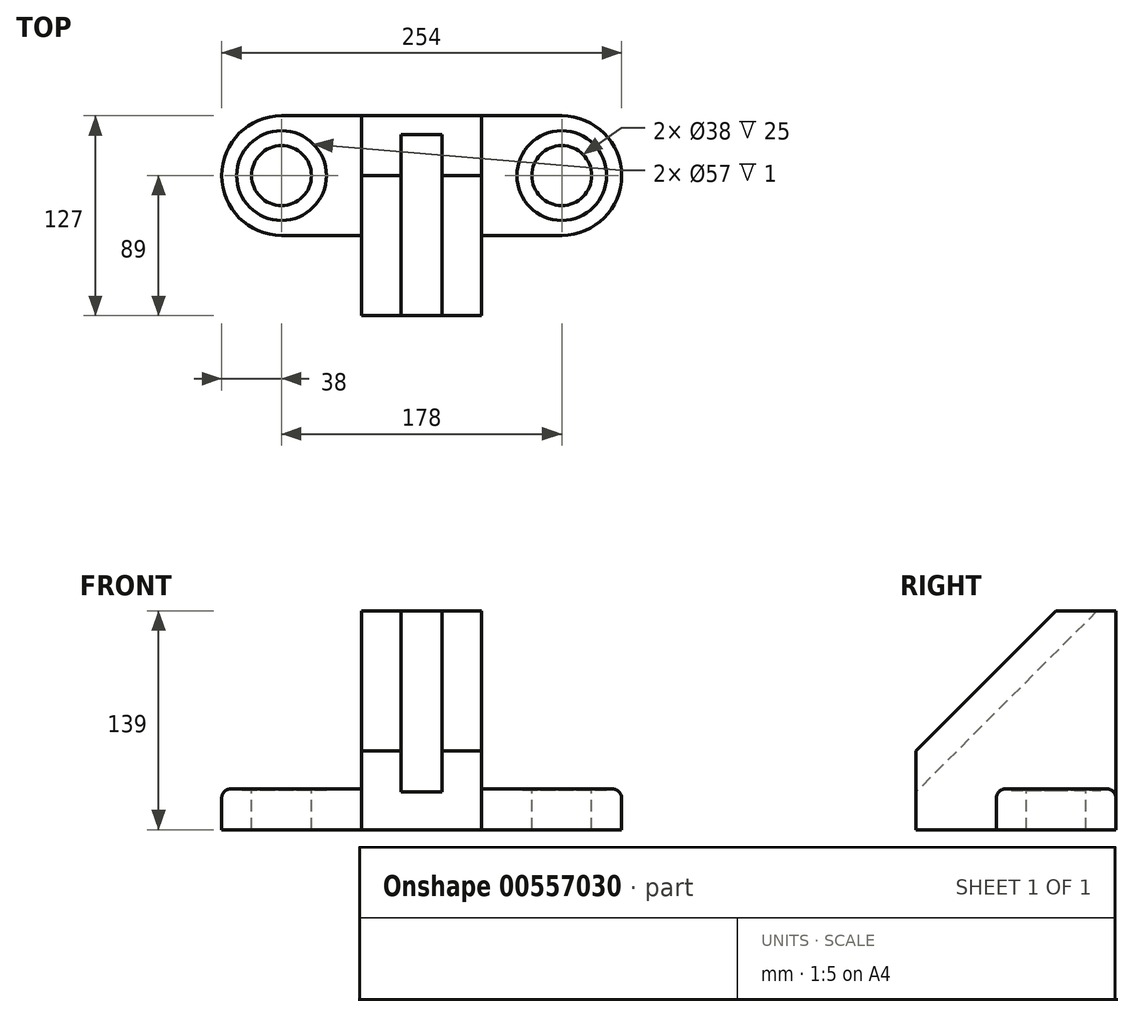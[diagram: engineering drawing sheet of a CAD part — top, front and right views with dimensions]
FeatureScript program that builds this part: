
annotation { "Feature Type Name" : "Feature", "Feature Type Description" : "" }
export const myFeature = defineFeature(function(context is Context, id is Id, definition is map)
    precondition{}
    {
        {
            var Q0;
            Q0=qCreatedBy(makeId("Right.planeOp"),FACE);
            var sketch = newSketch(context, id + "F0", { "sketchPlane" : qUnion([Q0])});
            skLineSegment(sketch, "E0.bottom", {"start": v(0, 0) * mm, "end": v(-127, 0) * mm});
            skLineSegment(sketch, "E0.top", {"start": v(0, -139) * mm, "end": v(-127, -139) * mm});
            skLineSegment(sketch, "E0.left", {"start": v(0, 0) * mm, "end": v(0, -139) * mm});
            skLineSegment(sketch, "E0.right", {"start": v(-127, 0) * mm, "end": v(-127, -139) * mm});
            skSolve(sketch);
        }
        {
            var Q0;
            Q0 = qSketchRegion(id + "F0", true);
            extrude(context, id + "F1", {"entities" : qUnion([Q0]), "depth" : 76 * mm, "offsetDistance" : 25 * mm});
        }
        {
            var Q0;
            Q0=makeQuery(id+"F1.opExtrude","CAP_FACE",FACE,{"disambiguationData":[OSD([sQuery(id+"F0.wireOp",EDGE,"E0.bottom"),sQuery(id+"F0.wireOp",EDGE,"E0.top"),sQuery(id+"F0.wireOp",EDGE,"E0.left"),sQuery(id+"F0.wireOp",EDGE,"E0.right")])],"isStart":true});
            var sketch = newSketch(context, id + "F2", { "sketchPlane" : qUnion([Q0])});
            skLineSegment(sketch, "E1.bottom", {"start": v(0, -139) * mm, "end": v(76, -139) * mm});
            skLineSegment(sketch, "E1.top", {"start": v(0, -113) * mm, "end": v(76, -113) * mm});
            skLineSegment(sketch, "E1.left", {"start": v(0, -139) * mm, "end": v(0, -113) * mm});
            skLineSegment(sketch, "E1.right", {"start": v(76, -139) * mm, "end": v(76, -113) * mm});
            skSolve(sketch);
        }
        {
            var Q0;
            Q0=makeQuery(id+"F1.opExtrude","CAP_FACE",FACE,{"disambiguationData":[OSD([sQuery(id+"F0.wireOp",EDGE,"E0.bottom"),sQuery(id+"F0.wireOp",EDGE,"E0.top"),sQuery(id+"F0.wireOp",EDGE,"E0.left"),sQuery(id+"F0.wireOp",EDGE,"E0.right")])],"isStart":false});
            var sketch = newSketch(context, id + "F3", { "sketchPlane" : qUnion([Q0])});
            skLineSegment(sketch, "E2.bottom", {"start": v(0, -139) * mm, "end": v(-76, -139) * mm});
            skLineSegment(sketch, "E2.top", {"start": v(0, -113) * mm, "end": v(-76, -113) * mm});
            skLineSegment(sketch, "E2.left", {"start": v(0, -139) * mm, "end": v(0, -113) * mm});
            skLineSegment(sketch, "E2.right", {"start": v(-76, -139) * mm, "end": v(-76, -113) * mm});
            skSolve(sketch);
        }
        {
            var Q0;
            Q0=makeQuery(id+"F3.imprint","IMPRINT",FACE,{"disambiguationData":[TD([[makeQuery(id+"F3.imprint","IMPRINT",EDGE,{"derivedFrom":sQuery(id+"F3.wireOp",EDGE,"E2.bottom")}),-1.0]])]});
            extrude(context, id + "F4", {"entities" : qUnion([Q0]), "operationType" : NewBodyOperationType.ADD, "depth" : 51 * mm, "offsetDistance" : 25 * mm});
        }
        {
            var Q0;
            Q0=makeQuery(id+"F2.imprint","IMPRINT",FACE,{"disambiguationData":[TD([[makeQuery(id+"F2.imprint","IMPRINT",EDGE,{"derivedFrom":sQuery(id+"F2.wireOp",EDGE,"E1.bottom")}),1.0]])]});
            extrude(context, id + "F5", {"entities" : qUnion([Q0]), "operationType" : NewBodyOperationType.ADD, "depth" : 51 * mm, "offsetDistance" : 25 * mm});
        }
        {
            var Q0;
            Q0=makeQuery(id+"F5.opExtrude","CAP_FACE",FACE,{"disambiguationData":[OSD([sQuery(id+"F2.wireOp",EDGE,"E1.bottom"),sQuery(id+"F2.wireOp",EDGE,"E1.top"),sQuery(id+"F2.wireOp",EDGE,"E1.left"),sQuery(id+"F2.wireOp",EDGE,"E1.right")])],"isStart":false});
            extrude(context, id + "F6", {"entities" : qUnion([Q0]), "operationType" : NewBodyOperationType.ADD, "depth" : 38 * mm, "offsetDistance" : 25 * mm});
        }
        {
            var Q0;
            Q0=makeQuery(id+"F4.opExtrude","CAP_FACE",FACE,{"disambiguationData":[OSD([sQuery(id+"F3.wireOp",EDGE,"E2.bottom"),sQuery(id+"F3.wireOp",EDGE,"E2.top"),sQuery(id+"F3.wireOp",EDGE,"E2.left"),sQuery(id+"F3.wireOp",EDGE,"E2.right")])],"isStart":false});
            extrude(context, id + "F7", {"entities" : qUnion([Q0]), "operationType" : NewBodyOperationType.ADD, "depth" : 38 * mm, "offsetDistance" : 25 * mm});
        }
        {
            var Q0;
            {var subQ0=sQuery(id+"F2.wireOp",EDGE,"E1.top");Q0=makeQuery(id+"F6.boolean.opBoolean","MERGE",FACE,{"derivedFrom":[makeQuery(id+"F5.opExtrude","SWEPT_FACE",FACE,{"disambiguationData":[OSD([subQ0])]}),makeQuery(id+"F6.opExtrude","SWEPT_FACE",FACE,{"disambiguationData":[OSD([subQ0])]})]});}
            var sketch = newSketch(context, id + "F8", { "sketchPlane" : qUnion([Q0])});
            skCircle(sketch, "E3", {"center": v(-51, -38) * mm, "radius": 19 * mm});
            skCircle(sketch, "E4", {"center": v(127, -38) * mm, "radius": 19 * mm});
            skSolve(sketch);
        }
        {
            var Q0;
            Q0=makeQuery(id+"F8.imprint","IMPRINT",FACE,{"disambiguationData":[TD([[makeQuery(id+"F8.imprint","IMPRINT",EDGE,{"derivedFrom":sQuery(id+"F8.wireOp",EDGE,"E3")}),1.0]])]});
            var Q1;
            Q1=makeQuery(id+"F8.imprint","IMPRINT",FACE,{"disambiguationData":[TD([[makeQuery(id+"F8.imprint","IMPRINT",EDGE,{"derivedFrom":sQuery(id+"F8.wireOp",EDGE,"E4")}),1.0]])]});
            extrude(context, id + "F9", {"entities" : qUnion([Q0, Q1]), "operationType" : NewBodyOperationType.REMOVE, "endBound" : BoundingType.THROUGH_ALL, "oppositeDirection" : true, "depth" : 25 * mm, "offsetDistance" : 25 * mm});
        }
        {
            var Q0;
            Q0=makeQuery(id+"F6.opExtrude","CAP_EDGE",EDGE,{"disambiguationData":[OSD([sQuery(id+"F2.wireOp",EDGE,"E1.left")])],"isStart":false});
            var Q1;
            Q1=makeQuery(id+"F6.opExtrude","CAP_EDGE",EDGE,{"disambiguationData":[OSD([sQuery(id+"F2.wireOp",EDGE,"E1.right")])],"isStart":false});
            var Q2;
            Q2=makeQuery(id+"F7.opExtrude","CAP_EDGE",EDGE,{"disambiguationData":[OSD([sQuery(id+"F3.wireOp",EDGE,"E2.right")])],"isStart":false});
            var Q3;
            Q3=makeQuery(id+"F7.opExtrude","CAP_EDGE",EDGE,{"disambiguationData":[OSD([sQuery(id+"F3.wireOp",EDGE,"E2.left")])],"isStart":false});
            fillet(context, id + "F10", {"entities" : qUnion([Q0, Q1, Q2, Q3]), "radius" : 38 * mm, "tangentPropagation" : true, "allowEdgeOverflow" : false});
        }
        {
            var Q0;
            {var subQ0=sQuery(id+"F2.wireOp",EDGE,"E1.top");Q0=makeQuery(id+"F6.boolean.opBoolean","MERGE",FACE,{"derivedFrom":[makeQuery(id+"F5.opExtrude","SWEPT_FACE",FACE,{"disambiguationData":[OSD([subQ0])]}),makeQuery(id+"F6.opExtrude","SWEPT_FACE",FACE,{"disambiguationData":[OSD([subQ0])]})]});}
            var sketch = newSketch(context, id + "F11", { "sketchPlane" : qUnion([Q0])});
            skCircle(sketch, "E5", {"center": v(-51, -38) * mm, "radius": 28.5 * mm});
            skSolve(sketch);
        }
        {
            var Q0;
            {var subQ0=sQuery(id+"F3.wireOp",EDGE,"E2.top");Q0=makeQuery(id+"F7.boolean.opBoolean","MERGE",FACE,{"derivedFrom":[makeQuery(id+"F4.opExtrude","SWEPT_FACE",FACE,{"disambiguationData":[OSD([subQ0])]}),makeQuery(id+"F7.opExtrude","SWEPT_FACE",FACE,{"disambiguationData":[OSD([subQ0])]})]});}
            var sketch = newSketch(context, id + "F12", { "sketchPlane" : qUnion([Q0])});
            skCircle(sketch, "E6", {"center": v(127, -38) * mm, "radius": 28.5 * mm});
            skSolve(sketch);
        }
        {
            var Q0;
            Q0=makeQuery(id+"F11.imprint","IMPRINT",FACE,{"disambiguationData":[TD([[makeQuery(id+"F11.imprint","IMPRINT",EDGE,{"derivedFrom":sQuery(id+"F11.wireOp",EDGE,"E5")}),1.0]])]});
            extrude(context, id + "F13", {"entities" : qUnion([Q0]), "operationType" : NewBodyOperationType.REMOVE, "oppositeDirection" : true, "depth" : 1 * mm, "offsetDistance" : 25 * mm});
        }
        {
            var Q0;
            Q0=makeQuery(id+"F12.imprint","IMPRINT",FACE,{"disambiguationData":[TD([[makeQuery(id+"F12.imprint","IMPRINT",EDGE,{"derivedFrom":sQuery(id+"F12.wireOp",EDGE,"E6")}),1.0]])]});
            extrude(context, id + "F14", {"entities" : qUnion([Q0]), "operationType" : NewBodyOperationType.REMOVE, "oppositeDirection" : true, "depth" : 1 * mm, "offsetDistance" : 25 * mm});
        }
        {
            var Q0;
            {var subQ0=sQuery(id+"F2.wireOp",EDGE,"E1.right");var subQ1=sQuery(id+"F2.wireOp",EDGE,"E1.top");Q0=makeQuery(id+"F6.boolean.opBoolean","MERGE",EDGE,{"derivedFrom":[makeQuery(id+"F5.opExtrude","SWEPT_EDGE",EDGE,{"disambiguationData":[OSD([subQ1,subQ0])]}),makeQuery(id+"F6.opExtrude","SWEPT_EDGE",EDGE,{"disambiguationData":[OSD([subQ1,subQ0])]})]});}
            var Q1;
            {var subQ0=sQuery(id+"F2.wireOp",EDGE,"E1.top");Q1=makeQuery(id+"F10.opFillet","BLEND_EDGE",EDGE,{"blendedFrom":[makeQuery(id+"F6.opExtrude","CAP_EDGE",EDGE,{"disambiguationData":[OSD([sQuery(id+"F2.wireOp",EDGE,"E1.left")])],"isStart":false}),makeQuery(id+"F6.boolean.opBoolean","MERGE",FACE,{"derivedFrom":[makeQuery(id+"F5.opExtrude","SWEPT_FACE",FACE,{"disambiguationData":[OSD([subQ0])]}),makeQuery(id+"F6.opExtrude","SWEPT_FACE",FACE,{"disambiguationData":[OSD([subQ0])]})]})],"blendedInto":[makeQuery(id+"F6.boolean.opBoolean","MERGE",FACE,{"derivedFrom":[makeQuery(id+"F5.opExtrude","SWEPT_FACE",FACE,{"disambiguationData":[OSD([subQ0])]}),makeQuery(id+"F6.opExtrude","SWEPT_FACE",FACE,{"disambiguationData":[OSD([subQ0])]})]})]});}
            var Q2;
            {var subQ0=sQuery(id+"F3.wireOp",EDGE,"E2.right");var subQ1=sQuery(id+"F3.wireOp",EDGE,"E2.top");Q2=makeQuery(id+"F7.boolean.opBoolean","MERGE",EDGE,{"derivedFrom":[makeQuery(id+"F4.opExtrude","SWEPT_EDGE",EDGE,{"disambiguationData":[OSD([subQ1,subQ0])]}),makeQuery(id+"F7.opExtrude","SWEPT_EDGE",EDGE,{"disambiguationData":[OSD([subQ1,subQ0])]})]});}
            fillet(context, id + "F15", {"entities" : qUnion([Q0, Q1, Q2]), "radius" : 6 * mm, "tangentPropagation" : true, "allowEdgeOverflow" : false});
        }
        {
            var Q0;
            Q0=makeQuery(id+"F1.opExtrude","CAP_FACE",FACE,{"disambiguationData":[OSD([sQuery(id+"F0.wireOp",EDGE,"E0.bottom"),sQuery(id+"F0.wireOp",EDGE,"E0.top"),sQuery(id+"F0.wireOp",EDGE,"E0.left"),sQuery(id+"F0.wireOp",EDGE,"E0.right")])],"isStart":true});
            var sketch = newSketch(context, id + "F16", { "sketchPlane" : qUnion([Q0])});
            skLineSegment(sketch, "E7", {"start": v(38, 0) * mm, "end": v(127, -89) * mm});
            skSolve(sketch);
        }
        {
            var Q0;
            {var subQ0=sQuery(id+"F16.wireOp",EDGE,"E7");Q0=makeQuery(id+"F16.imprint","IMPRINT",FACE,{"disambiguationData":[TD([[makeQuery(id+"F16.imprint","IMPRINT",EDGE,{"derivedFrom":subQ0}),1.0]])]});}
            extrude(context, id + "F17", {"entities" : qUnion([Q0]), "operationType" : NewBodyOperationType.REMOVE, "endBound" : BoundingType.THROUGH_ALL, "oppositeDirection" : true, "depth" : 25 * mm, "offsetDistance" : 25 * mm});
        }
        {
            var Q0;
            Q0=makeQuery(id+"F17.boolean.opBoolean","COPY",FACE,{"derivedFrom":makeQuery(id+"F17.opExtrude","SWEPT_FACE",FACE,{"disambiguationData":[OSD([sQuery(id+"F16.wireOp",EDGE,"E7")])]})});
            var sketch = newSketch(context, id + "F18", { "sketchPlane" : qUnion([Q0])});
            skLineSegment(sketch, "E8.bottom", {"start": v(25, -26.87) * mm, "end": v(51, -26.87) * mm});
            skLineSegment(sketch, "E8.top", {"start": v(25, -152.74) * mm, "end": v(51, -152.74) * mm});
            skLineSegment(sketch, "E8.left", {"start": v(25, -26.87) * mm, "end": v(25, -152.74) * mm});
            skLineSegment(sketch, "E8.right", {"start": v(51, -26.87) * mm, "end": v(51, -152.74) * mm});
            skSolve(sketch);
        }
        {
            var Q0;
            Q0=makeQuery(id+"F1.opExtrude","SWEPT_FACE",FACE,{"disambiguationData":[OSD([sQuery(id+"F0.wireOp",EDGE,"E0.bottom")])]});
            var sketch = newSketch(context, id + "F19", { "sketchPlane" : qUnion([Q0])});
            skLineSegment(sketch, "E9.bottom", {"start": v(25, -38) * mm, "end": v(51, -38) * mm});
            skLineSegment(sketch, "E9.top", {"start": v(25, -12) * mm, "end": v(51, -12) * mm});
            skLineSegment(sketch, "E9.left", {"start": v(25, -38) * mm, "end": v(25, -12) * mm});
            skLineSegment(sketch, "E9.right", {"start": v(51, -38) * mm, "end": v(51, -12) * mm});
            skSolve(sketch);
        }
        {
            var Q0;
            Q0=makeQuery(id+"F1.opExtrude","CAP_FACE",FACE,{"disambiguationData":[OSD([sQuery(id+"F0.wireOp",EDGE,"E0.bottom"),sQuery(id+"F0.wireOp",EDGE,"E0.top"),sQuery(id+"F0.wireOp",EDGE,"E0.left"),sQuery(id+"F0.wireOp",EDGE,"E0.right")])],"isStart":true});
            var sketch = newSketch(context, id + "F20", { "sketchPlane" : qUnion([Q0])});
            skLineSegment(sketch, "E10", {"start": v(12, 0) * mm, "end": v(127, -115) * mm});
            skSolve(sketch);
        }
        {
            var Q0;
            Q0=makeQuery(id+"F18.imprint","IMPRINT",FACE,{"disambiguationData":[TD([[makeQuery(id+"F18.imprint","IMPRINT",EDGE,{"derivedFrom":sQuery(id+"F18.wireOp",EDGE,"E8.bottom")}),1.0]])]});
            var Q1;
            Q1=sQuery(id+"F20.wireOp",VERTEX,"E10.start");
            extrude(context, id + "F21", {"entities" : qUnion([Q0]), "operationType" : NewBodyOperationType.REMOVE, "endBound" : BoundingType.UP_TO_VERTEX, "oppositeDirection" : true, "depth" : 25 * mm, "endBoundEntityVertex" : qUnion([Q1]), "offsetDistance" : 25 * mm});
        }
        {
            var Q0;
            Q0=makeQuery(id+"F21.boolean.opBoolean","COPY",FACE,{"derivedFrom":makeQuery(id+"F21.opExtrude","SWEPT_FACE",FACE,{"disambiguationData":[OSD([sQuery(id+"F18.wireOp",EDGE,"E8.bottom")])]})});
            extrude(context, id + "F22", {"entities" : qUnion([Q0]), "operationType" : NewBodyOperationType.REMOVE, "endBound" : BoundingType.THROUGH_ALL, "oppositeDirection" : true, "depth" : 25 * mm, "offsetDistance" : 25 * mm});
        }
        {
            var Q0;
            Q0=makeQuery(id+"F21.boolean.opBoolean","COPY",FACE,{"derivedFrom":makeQuery(id+"F21.opExtrude","SWEPT_FACE",FACE,{"disambiguationData":[OSD([sQuery(id+"F18.wireOp",EDGE,"E8.top")])]})});
            extrude(context, id + "F23", {"entities" : qUnion([Q0]), "operationType" : NewBodyOperationType.REMOVE, "endBound" : BoundingType.THROUGH_ALL, "oppositeDirection" : true, "depth" : 25 * mm, "offsetDistance" : 25 * mm});
        }
    });
